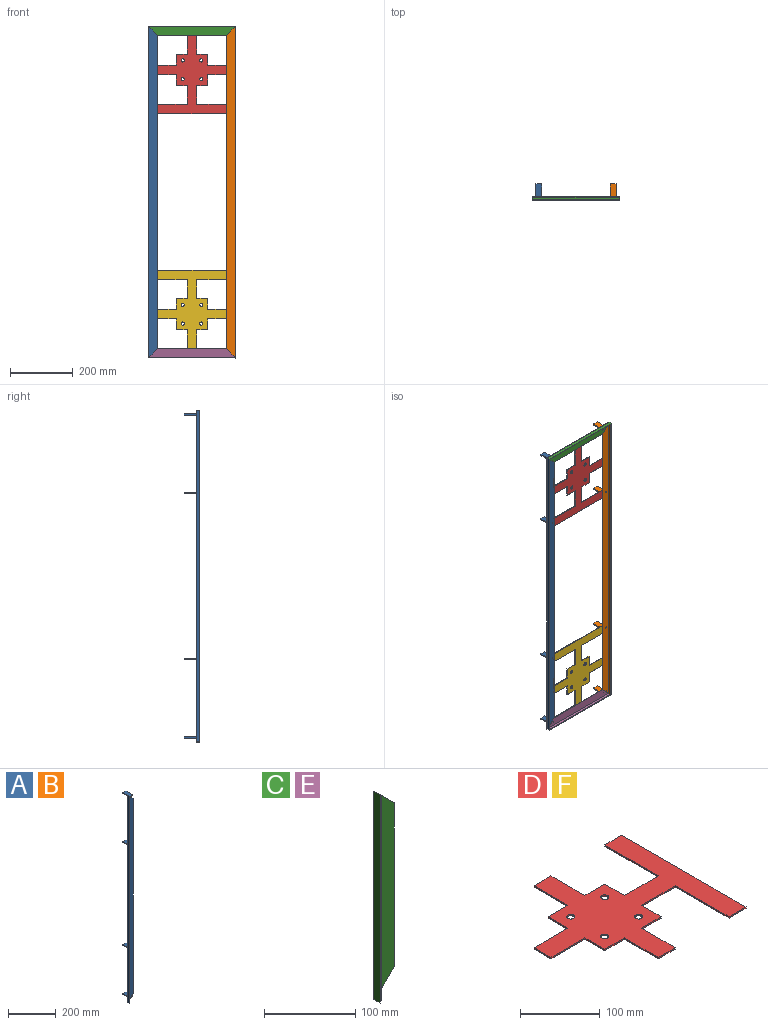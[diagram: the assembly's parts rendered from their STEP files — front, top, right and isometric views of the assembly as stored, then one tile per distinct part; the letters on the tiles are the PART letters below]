
ASSEMBLY  parts=6 mates=4
PART A: 28 faces, bbox 30x50x1060 mm
  f0: plane 1060x30mm, normal (0,1,0), area 30738.4mm2, adj f1,f5,f6,f7,f8,f9,f10,f12
  f1: plane 1060x10mm, normal (-1,0,0), area 10600mm2, adj f0,f2,f6,f7
  f2: plane 1060x2mm, normal (0,-1,0), area 2116mm2, adj f1,f3,f6,f7
  f3: plane 1056x8mm, normal (1,0,0), area 8448mm2, adj f2,f4,f6,f7
  f4: plane 1056x28mm, normal (0,-1,0), area 28784mm2, adj f3,f5,f6,f7
  f5: plane 1000x42mm, normal (1,0,0), area 2320mm2, adj f0,f4,f6,f7,f8,f9,f11,f12
  f6: plane 30x30mm, normal (0.71,0,-0.71), area 107.5mm2, adj f0,f1,f2,f3,f4,f5,f16
  f7: plane 30x30mm, normal (0.71,0,0.71), area 107.5mm2, adj f0,f1,f2,f3,f4,f5,f22
  f8: plane 40x18mm, normal (0,0,1), area 720mm2, adj f0,f5,f10,f11
  f9: plane 40x18mm, normal (0,0,-1), area 720mm2, adj f0,f5,f10,f11
  f10: plane 40x4mm, normal (-1,0,0), area 160mm2, adj f0,f8,f9,f11
  f11: plane 18x4mm, normal (0,1,0), area 72mm2, adj f5,f8,f9,f10
  f12: plane 40x18mm, normal (0,0,1), area 720mm2, adj f0,f5,f14,f15
  f13: plane 40x18mm, normal (0,0,-1), area 720mm2, adj f0,f5,f14,f15
  f14: plane 40x4mm, normal (-1,0,0), area 160mm2, adj f0,f12,f13,f15
  f15: plane 18x4mm, normal (0,1,0), area 72mm2, adj f5,f12,f13,f14
  f16: plane 17.8x4mm, normal (0,-1,0), area 63.2mm2, adj f6,f17,f19,f20
  f17: plane 40x18mm, normal (0,0,-1), area 720mm2, adj f0,f16,f18,f20,f21
  f18: plane 40x4mm, normal (-1,0,0), area 160mm2, adj f0,f17,f19,f21
  f19: plane 40x18mm, normal (0,0,1), area 720mm2, adj f0,f16,f18,f20,f21
  f20: plane 40x4mm, normal (1,0,0), area 160mm2, adj f16,f17,f19,f21
  f21: plane 18x4mm, normal (0,1,0), area 72mm2, adj f17,f18,f19,f20
  f22: plane 17.8x4mm, normal (0,-1,0), area 63.2mm2, adj f7,f23,f24,f25
  f23: plane 40x18mm, normal (0,0,1), area 720mm2, adj f0,f22,f24,f26,f27
  f24: plane 40x4mm, normal (1,0,0), area 160mm2, adj f22,f23,f25,f27
  f25: plane 40x18mm, normal (0,0,-1), area 720mm2, adj f0,f22,f24,f26,f27
  f26: plane 40x4mm, normal (-1,0,0), area 160mm2, adj f0,f23,f25,f27
  f27: plane 18x4mm, normal (0,1,0), area 72mm2, adj f23,f24,f25,f26
PART B: same geometry as A
PART C: 8 faces, bbox 30x10x280 mm
  f0: plane 280x30mm, normal (0,1,0), area 7500mm2, adj f1,f5,f6,f7
  f1: plane 280x10mm, normal (-1,0,0), area 2800mm2, adj f0,f2,f6,f7
  f2: plane 280x2mm, normal (0,-1,0), area 556mm2, adj f1,f3,f6,f7
  f3: plane 276x8mm, normal (1,0,0), area 2208mm2, adj f2,f4,f6,f7
  f4: plane 276x28mm, normal (0,-1,0), area 6944mm2, adj f3,f5,f6,f7
  f5: plane 220x2mm, normal (1,0,0), area 440mm2, adj f0,f4,f6,f7
  f6: plane 30x30mm, normal (0.71,0,-0.71), area 107.5mm2, adj f0,f1,f2,f3,f4,f5
  f7: plane 30x30mm, normal (0.71,0,0.71), area 107.5mm2, adj f0,f1,f2,f3,f4,f5
PART D: 30 faces, bbox 250x220x2 mm
  f0: plane 60x2mm, normal (-1,0,0), area 120mm2, adj f1,f26,f28,f29
  f1: plane 35x2mm, normal (0,1,0), area 70mm2, adj f0,f2,f28,f29
  f2: plane 35x2mm, normal (-1,0,0), area 70mm2, adj f1,f3,f28,f29
  f3: plane 60x2mm, normal (0,1,0), area 120mm2, adj f2,f4,f28,f29
  f4: plane 30x2mm, normal (-1,0,0), area 60mm2, adj f3,f5,f28,f29
  f5: plane 60x2mm, normal (0,-1,0), area 120mm2, adj f4,f6,f28,f29
  f6: plane 35x2mm, normal (-1,0,0), area 70mm2, adj f5,f7,f28,f29
  f7: plane 35x2mm, normal (0,-1,0), area 70mm2, adj f6,f8,f28,f29
  f8: plane 60x2mm, normal (-1,0,0), area 120mm2, adj f7,f9,f28,f29
  f9: plane 30x2mm, normal (0,-1,0), area 60mm2, adj f8,f10,f28,f29
  f10: plane 60x2mm, normal (1,0,0), area 120mm2, adj f9,f11,f28,f29
  f11: plane 35x2mm, normal (0,-1,0), area 70mm2, adj f10,f12,f28,f29
  f12: plane 35x2mm, normal (1,0,0), area 70mm2, adj f11,f13,f28,f29
  f13: plane 60x2mm, normal (0,-1,0), area 120mm2, adj f12,f14,f28,f29
  f14: plane 95x2mm, normal (-1,0,0), area 190mm2, adj f13,f15,f28,f29
  f15: plane 30x2mm, normal (0,-1,0), area 60mm2, adj f14,f16,f28,f29
  f16: plane 220x2mm, normal (1,0,0), area 440mm2, adj f15,f17,f28,f29
  f17: plane 30x2mm, normal (0,1,0), area 60mm2, adj f16,f18,f28,f29
  f18: plane 95x2mm, normal (-1,0,0), area 190mm2, adj f17,f19,f28,f29
  f19: plane 60x2mm, normal (0,1,0), area 120mm2, adj f18,f20,f28,f29
  f20: plane 35x2mm, normal (1,0,0), area 70mm2, adj f19,f21,f28,f29
  f21: plane 35x2mm, normal (0,1,0), area 70mm2, adj f20,f22,f28,f29
  f22: plane 60x2mm, normal (1,0,0), area 120mm2, adj f21,f26,f28,f29
  f23: cylinder r=5mm len=10mm, axis (0,0,-1), area 62.8mm2, adj f28,f29
  f24: cylinder r=5mm len=10mm, axis (0,0,-1), area 62.8mm2, adj f28,f29
  f25: cylinder r=5mm len=10mm, axis (0,0,-1), area 62.8mm2, adj f28,f29
  f26: plane 30x2mm, normal (0,1,0), area 60mm2, adj f0,f22,f28,f29
  f27: cylinder r=5mm len=10mm, axis (0,0,-1), area 62.8mm2, adj f28,f29
  f28: plane 250x220mm, normal (0,0,1), area 23485.8mm2, adj f0,f1,f2,f3,f4,f5,f6,f7
  f29: plane 250x220mm, normal (0,0,-1), area 23485.8mm2, adj f0,f1,f2,f3,f4,f5,f6,f7
PART E: same geometry as C
PART F: same geometry as D
PLACE A at identity
PLACE B rot(axis=(0,-1,0),180deg) t=(280,0,1060)mm
PLACE C rot(axis=(0,1,0),90deg) t=(0,0,1060)mm
PLACE D rot(axis=(-0.58,0.58,0.58),120deg) t=(67.66,-2,970)mm
PLACE E rot(axis=(0,-1,0),90deg) t=(280,0,0)mm
PLACE F rot(axis=(-0.58,-0.58,-0.58),120deg) t=(212.34,-2,90)mm
MATE fastened F.f4 <-> E.f5  axis (0,0,-1) through (140,-2,30)mm
MATE fastened D.f4 <-> C.f5  axis (0,0,1) through (140,-2,1030)mm
MATE fastened C.f6 <-> A.f7  axis (-0.71,0,-0.71) through (0,0,1060)mm
MATE fastened E.f7 <-> A.f6  axis (-0.71,0,0.71) through (0,0,0)mm
